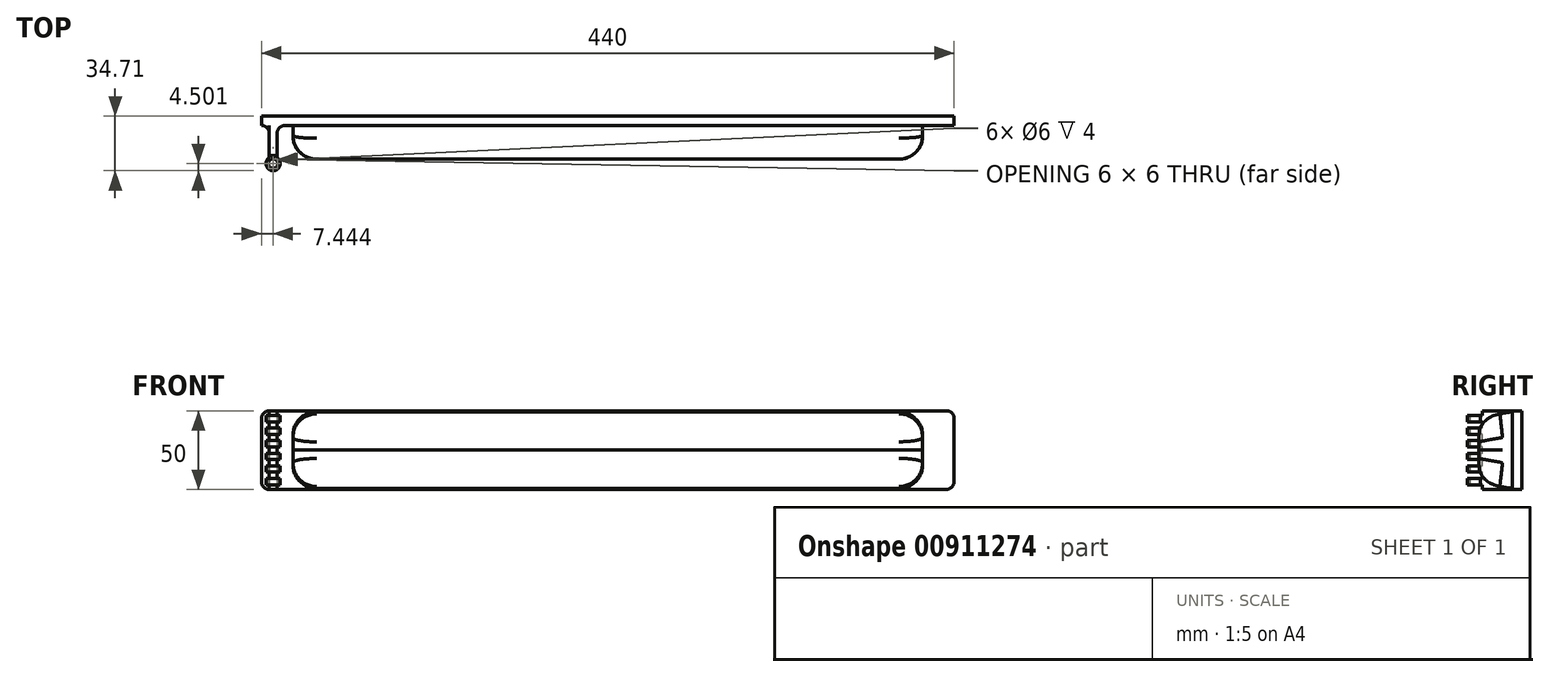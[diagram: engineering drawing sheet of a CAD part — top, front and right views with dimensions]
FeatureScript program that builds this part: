
annotation { "Feature Type Name" : "Feature", "Feature Type Description" : "" }
export const myFeature = defineFeature(function(context is Context, id is Id, definition is map)
    precondition{}
    {
        {
            var Q0;
            Q0=qCreatedBy(makeId("Front.planeOp"),FACE);
            var sketch = newSketch(context, id + "F0", { "sketchPlane" : qUnion([Q0])});
            skLineSegment(sketch, "E0", {"start": v(0, 0) * mm, "end": v(215, 0) * mm});
            skLineSegment(sketch, "E1.MirrorCS", {"start": v(0, 0) * mm, "end": v(-215, 0) * mm});
            skLineSegment(sketch, "E2", {"start": v(-220, 5) * mm, "end": v(-220, 45) * mm});
            skLineSegment(sketch, "E3.MirrorCS", {"start": v(220, 5) * mm, "end": v(220, 45) * mm});
            skLineSegment(sketch, "E4", {"start": v(-215, 50) * mm, "end": v(215, 50) * mm});
            skPoint(sketch, "E5.visualSharp", {"position": v(-220, 50) * mm});
            skArc(sketch, "E5.filletArc", {"start": v(-215, 50) * mm, "mid": v(-218.54, 48.54) * mm, "end": v(-220, 45) * mm});
            skPoint(sketch, "E6.visualSharp", {"position": v(-220, 0) * mm});
            skArc(sketch, "E6.filletArc", {"start": v(-220, 5) * mm, "mid": v(-218.54, 1.46) * mm, "end": v(-215, 0) * mm});
            skPoint(sketch, "E7.visualSharp", {"position": v(220, 50) * mm});
            skArc(sketch, "E7.filletArc", {"start": v(220, 45) * mm, "mid": v(218.54, 48.54) * mm, "end": v(215, 50) * mm});
            skPoint(sketch, "E8.visualSharp", {"position": v(220, 0) * mm});
            skArc(sketch, "E8.filletArc", {"start": v(215, 0) * mm, "mid": v(218.54, 1.46) * mm, "end": v(220, 5) * mm});
            skPoint(sketch, "E9.start.orphan", {"position": v(0, 76.62) * mm});
            skSolve(sketch);
        }
        {
            var Q0;
            Q0=makeQuery(id+"F0.imprint","IMPRINT",FACE,{"disambiguationData":[TD([[makeQuery(id+"F0.imprint","IMPRINT",EDGE,{"derivedFrom":sQuery(id+"F0.wireOp",EDGE,"E0")}),1.0]])]});
            extrude(context, id + "F1", {"entities" : qUnion([Q0]), "depth" : 6 * mm, "offsetDistance" : 25 * mm});
        }
        {
            var Q0;
            Q0=qCreatedBy(makeId("Right.planeOp"),FACE);
            var sketch = newSketch(context, id + "F2", { "sketchPlane" : qUnion([Q0])});
            skLineSegment(sketch, "E10", {"start": v(0, 0) * mm, "end": v(0, 25) * mm});
            skLineSegment(sketch, "E11", {"start": v(0, 25) * mm, "end": v(-6.05, 25) * mm});
            skFitSpline(sketch, "E12", {"points": [v(-27.4, 25) * mm, v(-26.12, 39.67) * mm, v(-20.72, 45.62) * mm, v(-6.05, 49.35) * mm], "startDerivative": vector(0.8, 82.21) * mm, "endDerivative": vector(47.14, 6.19) * mm});
            skFitSpline(sketch, "E13.MirrorCS", {"points": [v(-27.4, 25) * mm, v(-26.12, 10.33) * mm, v(-20.72, 4.38) * mm, v(-6.05, 0.65) * mm], "startDerivative": vector(0.8, -82.21) * mm, "endDerivative": vector(47.14, -6.19) * mm});
            skLineSegment(sketch, "E14", {"start": v(-6.05, 49.35) * mm, "end": v(-6.05, 0.65) * mm});
            skSolve(sketch);
        }
        {
            var Q0;
            Q0 = qSketchRegion(id + "F2", true);
            extrude(context, id + "F3", {"entities" : qUnion([Q0]), "endBound" : BoundingType.SYMMETRIC, "depth" : 400 * mm, "offsetDistance" : 25 * mm});
        }
        {
            var Q0;
            Q0=qCreatedBy(makeId("Top.planeOp"),FACE);
            cPlane(context, id + "F4", {"entities" : qUnion([Q0]), "cplaneType" : CPlaneType.OFFSET, "offset" : 25 * mm, "width" : 150 * mm, "height" : 150 * mm});
        }
        {
            var Q0;
            Q0=makeQuery(id+"F3.opExtrude","CAP_EDGE",EDGE,{"disambiguationData":[OSD([sQuery(id+"F2.wireOp",EDGE,"E13.MirrorCS")])],"isStart":true});
            var Q1;
            Q1=makeQuery(id+"F3.opExtrude","CAP_EDGE",EDGE,{"disambiguationData":[OSD([sQuery(id+"F2.wireOp",EDGE,"E12")])],"isStart":true});
            var Q2;
            Q2=makeQuery(id+"F3.opExtrude","CAP_EDGE",EDGE,{"disambiguationData":[OSD([sQuery(id+"F2.wireOp",EDGE,"E13.MirrorCS")])],"isStart":false});
            var Q3;
            Q3=makeQuery(id+"F3.opExtrude","CAP_EDGE",EDGE,{"disambiguationData":[OSD([sQuery(id+"F2.wireOp",EDGE,"E12")])],"isStart":false});
            fillet(context, id + "F5", {"entities" : qUnion([Q0, Q1, Q2, Q3]), "radius" : 15 * mm, "tangentPropagation" : true, "allowEdgeOverflow" : false});
        }
        {
            var Q0;
            Q0=qCreatedBy(id+"F4.planeOp",FACE);
            var sketch = newSketch(context, id + "F6", { "sketchPlane" : qUnion([Q0])});
            skLineSegment(sketch, "E15", {"start": v(-212.56, -30.2) * mm, "end": v(-164.46, -30.2) * mm});
            skLineSegment(sketch, "E16", {"start": v(-164.46, -30.2) * mm, "end": v(-164.46, -25.2) * mm});
            skCircle(sketch, "E17", {"center": v(-212.56, -30.2) * mm, "radius": 3 * mm});
            skArc(sketch, "E18", {"start": v(-215.06, -26.47) * mm, "mid": v(-212.56, -34.7) * mm, "end": v(-210.06, -26.47) * mm});
            skLineSegment(sketch, "E19", {"start": v(-215.06, -26.47) * mm, "end": v(-215.06, 0) * mm});
            skLineSegment(sketch, "E20.MirrorCS", {"start": v(-210.06, -26.47) * mm, "end": v(-210.06, 0) * mm});
            skLineSegment(sketch, "E21", {"start": v(-215.06, 0) * mm, "end": v(-210.06, 0) * mm});
            skPoint(sketch, "E22.start.orphan", {"position": v(-212.56, 0) * mm});
            skSolve(sketch);
        }
        {
            var Q0;
            Q0 = qSketchRegion(id + "F6", true);
            extrude(context, id + "F7", {"entities" : qUnion([Q0]), "operationType" : NewBodyOperationType.ADD, "endBound" : BoundingType.SYMMETRIC, "depth" : 50 * mm, "offsetDistance" : 25 * mm});
        }
        {
            var Q0;
            Q0=makeQuery(id+"F7.boolean.opBoolean","INTERSECT",EDGE,{"derivedFrom":[makeQuery(id+"F1.opExtrude","CAP_FACE",FACE,{"disambiguationData":[OSD([sQuery(id+"F0.wireOp",EDGE,"E0"),sQuery(id+"F0.wireOp",EDGE,"E1.MirrorCS"),sQuery(id+"F0.wireOp",EDGE,"E2"),sQuery(id+"F0.wireOp",EDGE,"E3.MirrorCS"),sQuery(id+"F0.wireOp",EDGE,"E4"),sQuery(id+"F0.wireOp",EDGE,"E5.filletArc"),sQuery(id+"F0.wireOp",EDGE,"E6.filletArc"),sQuery(id+"F0.wireOp",EDGE,"E7.filletArc"),sQuery(id+"F0.wireOp",EDGE,"E8.filletArc")])],"isStart":false}),makeQuery(id+"F7.opExtrude","SWEPT_FACE",FACE,{"disambiguationData":[OSD([sQuery(id+"F6.wireOp",EDGE,"E20.MirrorCS")])]})]});
            var Q1;
            Q1=makeQuery(id+"F7.boolean.opBoolean","INTERSECT",EDGE,{"derivedFrom":[makeQuery(id+"F1.opExtrude","CAP_FACE",FACE,{"disambiguationData":[OSD([sQuery(id+"F0.wireOp",EDGE,"E0"),sQuery(id+"F0.wireOp",EDGE,"E1.MirrorCS"),sQuery(id+"F0.wireOp",EDGE,"E2"),sQuery(id+"F0.wireOp",EDGE,"E3.MirrorCS"),sQuery(id+"F0.wireOp",EDGE,"E4"),sQuery(id+"F0.wireOp",EDGE,"E5.filletArc"),sQuery(id+"F0.wireOp",EDGE,"E6.filletArc"),sQuery(id+"F0.wireOp",EDGE,"E7.filletArc"),sQuery(id+"F0.wireOp",EDGE,"E8.filletArc")])],"isStart":false}),makeQuery(id+"F7.opExtrude","SWEPT_FACE",FACE,{"disambiguationData":[OSD([sQuery(id+"F6.wireOp",EDGE,"E19")])]})]});
            fillet(context, id + "F8", {"entities" : qUnion([Q0, Q1]), "radius" : 5 * mm, "tangentPropagation" : true, "allowEdgeOverflow" : false});
        }
        {
            var Q0;
            Q0=qCreatedBy(makeId("Front.planeOp"),FACE);
            cPlane(context, id + "F9", {"entities" : qUnion([Q0]), "cplaneType" : CPlaneType.OFFSET, "offset" : 40 * mm, "width" : 150 * mm, "height" : 150 * mm});
        }
        {
            var Q0;
            Q0=qCreatedBy(id+"F9.planeOp",FACE);
            var sketch = newSketch(context, id + "F10", { "sketchPlane" : qUnion([Q0])});
            skLineSegment(sketch, "E23", {"start": v(-212.15, 25) * mm, "end": v(-212.15, 55) * mm});
            skLineSegment(sketch, "E24", {"start": v(-212.15, 27) * mm, "end": v(-217.2, 27) * mm});
            skLineSegment(sketch, "E25", {"start": v(-217.2, 27) * mm, "end": v(-217.2, 25) * mm});
            skLineSegment(sketch, "E26", {"start": v(-217.2, 27) * mm, "end": v(-217.2, 50.08) * mm});
            skLineSegment(sketch, "E27", {"start": v(-217.2, 31) * mm, "end": v(-212.15, 31) * mm});
            skLineSegment(sketch, "E28", {"start": v(-217.2, 35) * mm, "end": v(-212.15, 35) * mm});
            skLineSegment(sketch, "E29", {"start": v(-217.2, 39) * mm, "end": v(-212.15, 39) * mm});
            skLineSegment(sketch, "E30", {"start": v(-217.2, 43) * mm, "end": v(-212.15, 43) * mm});
            skLineSegment(sketch, "E31", {"start": v(-217.2, 47) * mm, "end": v(-212.15, 47) * mm});
            skLineSegment(sketch, "E32", {"start": v(-217.2, 51) * mm, "end": v(-212.15, 51) * mm});
            skLineSegment(sketch, "E33", {"start": v(-217.2, 51) * mm, "end": v(-217.2, 50.08) * mm});
            skLineSegment(sketch, "E34.MirrorCS", {"start": v(-207.1, 27) * mm, "end": v(-207.1, 50.08) * mm});
            skLineSegment(sketch, "E35.MirrorCS", {"start": v(-207.1, 51) * mm, "end": v(-207.1, 50.08) * mm});
            skLineSegment(sketch, "E36.MirrorCS", {"start": v(-207.1, 51) * mm, "end": v(-212.15, 51) * mm});
            skLineSegment(sketch, "E37.MirrorCS", {"start": v(-207.1, 47) * mm, "end": v(-212.15, 47) * mm});
            skLineSegment(sketch, "E38.MirrorCS", {"start": v(-207.1, 43) * mm, "end": v(-212.15, 43) * mm});
            skLineSegment(sketch, "E39.MirrorCS", {"start": v(-207.1, 39) * mm, "end": v(-212.15, 39) * mm});
            skLineSegment(sketch, "E40.MirrorCS", {"start": v(-207.1, 35) * mm, "end": v(-212.15, 35) * mm});
            skLineSegment(sketch, "E41.MirrorCS", {"start": v(-207.1, 31) * mm, "end": v(-212.15, 31) * mm});
            skLineSegment(sketch, "E42.MirrorCS", {"start": v(-212.15, 27) * mm, "end": v(-207.1, 27) * mm});
            skLineSegment(sketch, "E43.MirrorCS", {"start": v(-207.1, 27) * mm, "end": v(-207.1, 25) * mm});
            skLineSegment(sketch, "E44.MirrorCS", {"start": v(-212.15, 25) * mm, "end": v(-212.15, -5) * mm});
            skLineSegment(sketch, "E45.MirrorCS", {"start": v(-207.1, 23) * mm, "end": v(-207.1, -0.08) * mm});
            skLineSegment(sketch, "E46.MirrorCS", {"start": v(-217.2, 23) * mm, "end": v(-217.2, -0.08) * mm});
            skLineSegment(sketch, "E47.MirrorCS", {"start": v(-217.2, 23) * mm, "end": v(-217.2, 25) * mm});
            skLineSegment(sketch, "E48.MirrorCS", {"start": v(-207.1, 23) * mm, "end": v(-207.1, 25) * mm});
            skLineSegment(sketch, "E49.MirrorCS", {"start": v(-212.15, 23) * mm, "end": v(-207.1, 23) * mm});
            skLineSegment(sketch, "E50.MirrorCS", {"start": v(-212.15, 23) * mm, "end": v(-217.2, 23) * mm});
            skLineSegment(sketch, "E51.MirrorCS", {"start": v(-217.2, 19) * mm, "end": v(-212.15, 19) * mm});
            skLineSegment(sketch, "E52.MirrorCS", {"start": v(-217.2, 15) * mm, "end": v(-212.15, 15) * mm});
            skLineSegment(sketch, "E53.MirrorCS", {"start": v(-207.1, 15) * mm, "end": v(-212.15, 15) * mm});
            skLineSegment(sketch, "E54.MirrorCS", {"start": v(-207.1, 19) * mm, "end": v(-212.15, 19) * mm});
            skLineSegment(sketch, "E55.MirrorCS", {"start": v(-207.1, 11) * mm, "end": v(-212.15, 11) * mm});
            skLineSegment(sketch, "E56.MirrorCS", {"start": v(-217.2, 11) * mm, "end": v(-212.15, 11) * mm});
            skLineSegment(sketch, "E57.MirrorCS", {"start": v(-217.2, 7) * mm, "end": v(-212.15, 7) * mm});
            skLineSegment(sketch, "E58.MirrorCS", {"start": v(-207.1, 7) * mm, "end": v(-212.15, 7) * mm});
            skLineSegment(sketch, "E59.MirrorCS", {"start": v(-207.1, 3) * mm, "end": v(-212.15, 3) * mm});
            skLineSegment(sketch, "E60.MirrorCS", {"start": v(-217.2, 3) * mm, "end": v(-212.15, 3) * mm});
            skLineSegment(sketch, "E61.MirrorCS", {"start": v(-217.2, -1) * mm, "end": v(-217.2, -0.08) * mm});
            skLineSegment(sketch, "E62.MirrorCS", {"start": v(-217.2, -1) * mm, "end": v(-212.15, -1) * mm});
            skLineSegment(sketch, "E63.MirrorCS", {"start": v(-207.1, -1) * mm, "end": v(-207.1, -0.08) * mm});
            skLineSegment(sketch, "E64.MirrorCS", {"start": v(-207.1, -1) * mm, "end": v(-212.15, -1) * mm});
            skSolve(sketch);
        }
        {
            var Q0;
            {var subQ1=sQuery(id+"F10.wireOp",EDGE,"E31");Q0=makeQuery(id+"F10.imprint","IMPRINT",FACE,{"disambiguationData":[TD([[makeQuery(id+"F10.imprint","IMPRINT",EDGE,{"derivedFrom":subQ1}),1.0]])]});}
            var Q1;
            {var subQ1=sQuery(id+"F10.wireOp",EDGE,"E35.MirrorCS");Q1=makeQuery(id+"F10.imprint","IMPRINT",FACE,{"disambiguationData":[TD([[makeQuery(id+"F10.imprint","IMPRINT",EDGE,{"derivedFrom":subQ1}),-1.0]])]});}
            var Q2;
            {var subQ0=sQuery(id+"F10.wireOp",EDGE,"E29");Q2=makeQuery(id+"F10.imprint","IMPRINT",FACE,{"disambiguationData":[TD([[makeQuery(id+"F10.imprint","IMPRINT",EDGE,{"derivedFrom":subQ0}),1.0]])]});}
            var Q3;
            {var subQ2=sQuery(id+"F10.wireOp",EDGE,"E38.MirrorCS");Q3=makeQuery(id+"F10.imprint","IMPRINT",FACE,{"disambiguationData":[TD([[makeQuery(id+"F10.imprint","IMPRINT",EDGE,{"derivedFrom":subQ2}),1.0]])]});}
            var Q4;
            {var subQ0=sQuery(id+"F10.wireOp",EDGE,"E27");Q4=makeQuery(id+"F10.imprint","IMPRINT",FACE,{"disambiguationData":[TD([[makeQuery(id+"F10.imprint","IMPRINT",EDGE,{"derivedFrom":subQ0}),1.0]])]});}
            var Q5;
            {var subQ2=sQuery(id+"F10.wireOp",EDGE,"E40.MirrorCS");Q5=makeQuery(id+"F10.imprint","IMPRINT",FACE,{"disambiguationData":[TD([[makeQuery(id+"F10.imprint","IMPRINT",EDGE,{"derivedFrom":subQ2}),1.0]])]});}
            var Q6;
            {var subQ4=sQuery(id+"F10.wireOp",EDGE,"E42.MirrorCS");Q6=makeQuery(id+"F10.imprint","IMPRINT",FACE,{"disambiguationData":[TD([[makeQuery(id+"F10.imprint","IMPRINT",EDGE,{"derivedFrom":subQ4}),-1.0]])]});}
            var Q7;
            {var subQ4=sQuery(id+"F10.wireOp",EDGE,"E24");Q7=makeQuery(id+"F10.imprint","IMPRINT",FACE,{"disambiguationData":[TD([[makeQuery(id+"F10.imprint","IMPRINT",EDGE,{"derivedFrom":subQ4}),1.0]])]});}
            var Q8;
            {var subQ0=sQuery(id+"F10.wireOp",EDGE,"E51.MirrorCS");Q8=makeQuery(id+"F10.imprint","IMPRINT",FACE,{"disambiguationData":[TD([[makeQuery(id+"F10.imprint","IMPRINT",EDGE,{"derivedFrom":subQ0}),-1.0]])]});}
            var Q9;
            {var subQ2=sQuery(id+"F10.wireOp",EDGE,"E53.MirrorCS");Q9=makeQuery(id+"F10.imprint","IMPRINT",FACE,{"disambiguationData":[TD([[makeQuery(id+"F10.imprint","IMPRINT",EDGE,{"derivedFrom":subQ2}),-1.0]])]});}
            var Q10;
            {var subQ0=sQuery(id+"F10.wireOp",EDGE,"E55.MirrorCS");Q10=makeQuery(id+"F10.imprint","IMPRINT",FACE,{"disambiguationData":[TD([[makeQuery(id+"F10.imprint","IMPRINT",EDGE,{"derivedFrom":subQ0}),1.0]])]});}
            var Q11;
            {var subQ0=sQuery(id+"F10.wireOp",EDGE,"E56.MirrorCS");Q11=makeQuery(id+"F10.imprint","IMPRINT",FACE,{"disambiguationData":[TD([[makeQuery(id+"F10.imprint","IMPRINT",EDGE,{"derivedFrom":subQ0}),-1.0]])]});}
            var Q12;
            {var subQ0=sQuery(id+"F10.wireOp",EDGE,"E60.MirrorCS");Q12=makeQuery(id+"F10.imprint","IMPRINT",FACE,{"disambiguationData":[TD([[makeQuery(id+"F10.imprint","IMPRINT",EDGE,{"derivedFrom":subQ0}),-1.0]])]});}
            var Q13;
            {var subQ2=sQuery(id+"F10.wireOp",EDGE,"E59.MirrorCS");Q13=makeQuery(id+"F10.imprint","IMPRINT",FACE,{"disambiguationData":[TD([[makeQuery(id+"F10.imprint","IMPRINT",EDGE,{"derivedFrom":subQ2}),1.0]])]});}
            extrude(context, id + "F11", {"entities" : qUnion([Q0, Q1, Q2, Q3, Q4, Q5, Q6, Q7, Q8, Q9, Q10, Q11, Q12, Q13]), "operationType" : NewBodyOperationType.REMOVE, "oppositeDirection" : true, "depth" : 15 * mm, "offsetDistance" : 25 * mm});
        }
    });
